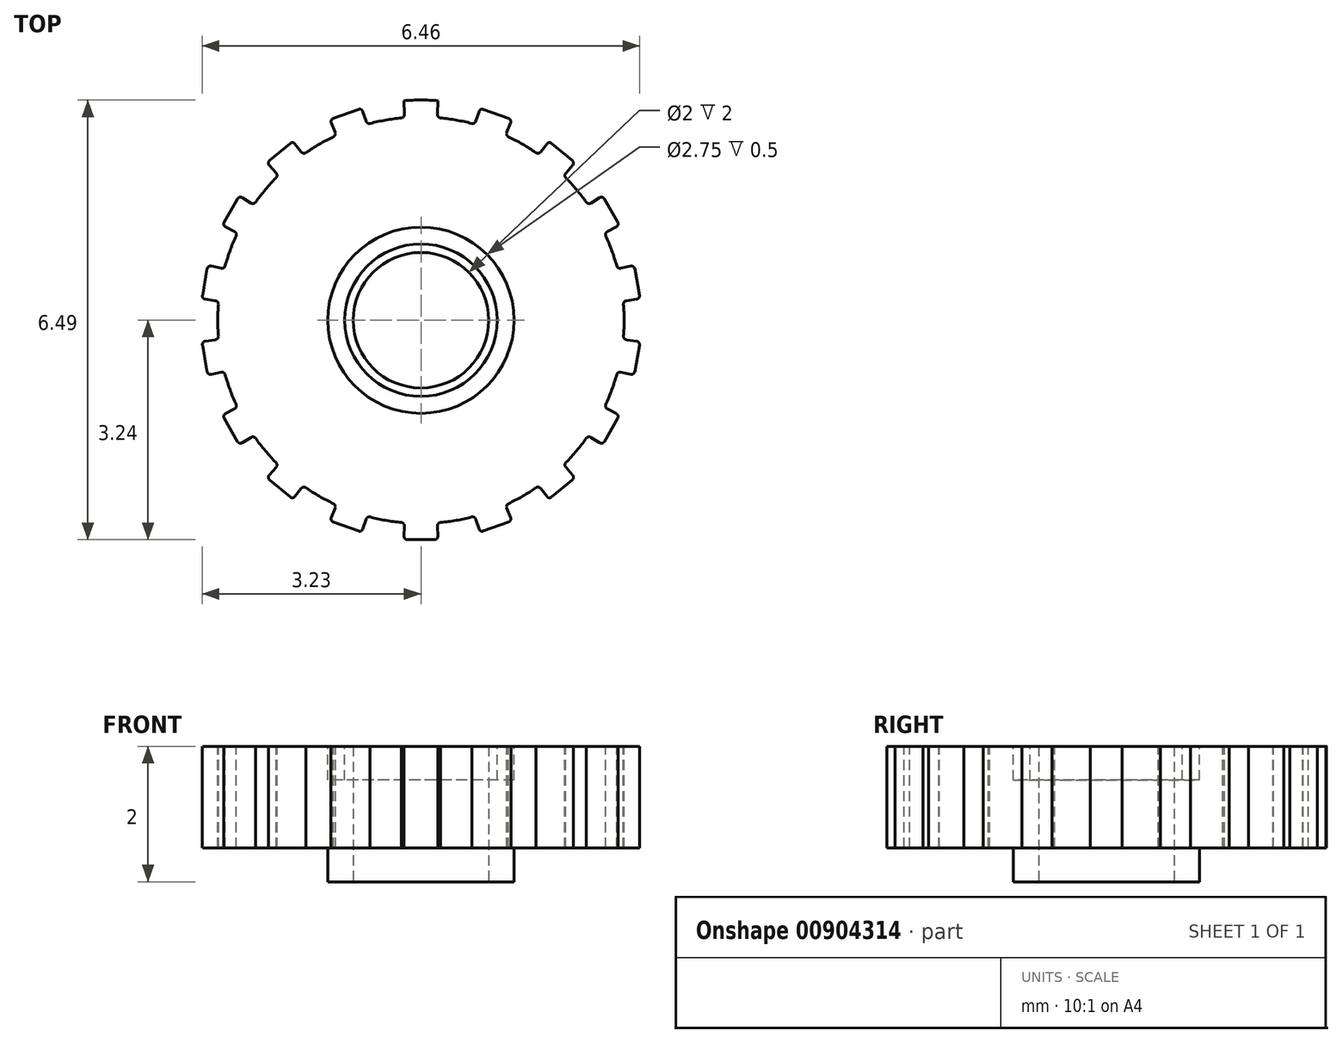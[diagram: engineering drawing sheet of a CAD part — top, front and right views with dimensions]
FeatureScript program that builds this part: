
annotation { "Feature Type Name" : "Feature", "Feature Type Description" : "" }
export const myFeature = defineFeature(function(context is Context, id is Id, definition is map)
    precondition{}
    {
        {
            var Q0;
            Q0=qCreatedBy(makeId("Front.planeOp"),FACE);
            var sketch = newSketch(context, id + "F0", { "sketchPlane" : qUnion([Q0])});
            skLineSegment(sketch, "E0.bottom", {"start": v(0, 0) * mm, "end": v(-3.25, 0) * mm});
            skLineSegment(sketch, "E0.top", {"start": v(0, 2) * mm, "end": v(-3.25, 2) * mm});
            skLineSegment(sketch, "E0.left", {"start": v(0, 0) * mm, "end": v(0, 2) * mm});
            skLineSegment(sketch, "E0.right", {"start": v(-3.25, 0) * mm, "end": v(-3.25, 2) * mm});
            skLineSegment(sketch, "E1", {"start": v(-1, 2) * mm, "end": v(-1, 0) * mm});
            skSolve(sketch);
        }
        {
            var Q0;
            {var subQ0=sQuery(id+"F0.wireOp",EDGE,"E0.right");Q0=makeQuery(id+"F0.imprint","IMPRINT",FACE,{"disambiguationData":[TD([[makeQuery(id+"F0.imprint","IMPRINT",EDGE,{"derivedFrom":subQ0}),-1.0]])]});}
            var Q1;
            Q1=sQuery(id+"F0.wireOp",EDGE,"E0.left");
            revolve(context, id + "F1", {"surfaceOperationType" : NewSurfaceOperationType.NEW, "entities" : qUnion([Q0]), "axis" : qUnion([Q1]), "revolveType" : RevolveType.FULL});
        }
        {
            var Q0;
            Q0=makeQuery(id+"F1.opRevolve","SWEPT_FACE",FACE,{"disambiguationData":[OSD([sQuery(id+"F0.wireOp",EDGE,"E0.top")])]});
            var sketch = newSketch(context, id + "F2", { "sketchPlane" : qUnion([Q0])});
            skLineSegment(sketch, "E2", {"start": v(0, 0) * mm, "end": v(0, 3.25) * mm});
            skLineSegment(sketch, "E3", {"start": v(0, 3.24) * mm, "end": v(-0.25, 3.24) * mm});
            skLineSegment(sketch, "E4", {"start": v(-0.25, 3.24) * mm, "end": v(0.25, 3.24) * mm});
            skLineSegment(sketch, "E5.bottom", {"start": v(0.12, 0) * mm, "end": v(-0.12, 0) * mm});
            skLineSegment(sketch, "E5.top", {"start": v(0.12, 0) * mm, "end": v(-0.12, 0) * mm});
            skLineSegment(sketch, "E5.left", {"start": v(0.12, 0) * mm, "end": v(0.12, 0) * mm});
            skLineSegment(sketch, "E5.right", {"start": v(-0.12, 0) * mm, "end": v(-0.12, 0) * mm});
            skPoint(sketch, "E5.middle", {"position": v(0, 0) * mm});
            skLineSegment(sketch, "E6", {"start": v(-0.25, 3.24) * mm, "end": v(-0.13, 0) * mm});
            skLineSegment(sketch, "E7", {"start": v(0.25, 3.24) * mm, "end": v(0.12, 0) * mm});
            skCircle(sketch, "E8", {"center": v(0, 0) * mm, "radius": 3 * mm});
            skLineSegment(sketch, "E9", {"start": v(-0.25, 3.24) * mm, "end": v(-0.2, 3.24) * mm});
            skLineSegment(sketch, "E10", {"start": v(-0.2, 3.24) * mm, "end": v(0.2, 3.24) * mm});
            skLineSegment(sketch, "E11", {"start": v(0.2, 3.24) * mm, "end": v(0.25, 3.24) * mm});
            skLineSegment(sketch, "E12", {"start": v(-0.2, 3.24) * mm, "end": v(-0.12, 0) * mm});
            skLineSegment(sketch, "E13", {"start": v(0.2, 3.24) * mm, "end": v(0.12, 0) * mm});
            skLineSegment(sketch, "E14", {"start": v(-0.25, 3.2) * mm, "end": v(0.25, 3.2) * mm});
            skLineSegment(sketch, "E15", {"start": v(-0.25, 3.2) * mm, "end": v(-0.3, 3.2) * mm});
            skLineSegment(sketch, "E16", {"start": v(0.25, 3.2) * mm, "end": v(0.3, 3.2) * mm});
            skLineSegment(sketch, "E17", {"start": v(-0.3, 3.2) * mm, "end": v(-0.13, 0) * mm});
            skLineSegment(sketch, "E18", {"start": v(0.3, 3.2) * mm, "end": v(0.13, 0) * mm});
            skLineSegment(sketch, "E19", {"start": v(-0.24, 3.04) * mm, "end": v(0.2, 3.04) * mm});
            skLineSegment(sketch, "E20", {"start": v(0.2, 3.04) * mm, "end": v(0.24, 3.04) * mm});
            skLineSegment(sketch, "E21", {"start": v(0.24, 3.04) * mm, "end": v(-0.2, 3.04) * mm});
            skArc(sketch, "E22", {"start": v(-0.29, 2.99) * mm, "mid": v(-0.25, 3) * mm, "end": v(-0.24, 3.04) * mm});
            skArc(sketch, "E23", {"start": v(-0.2, 3.24) * mm, "mid": v(-0.23, 3.23) * mm, "end": v(-0.25, 3.2) * mm});
            skArc(sketch, "E24", {"start": v(0.25, 3.2) * mm, "mid": v(0.23, 3.23) * mm, "end": v(0.2, 3.24) * mm});
            skArc(sketch, "E25", {"start": v(0.24, 3.04) * mm, "mid": v(0.25, 3) * mm, "end": v(0.29, 2.99) * mm});
            skArc(sketch, "E26.1.0", {"start": v(-1.3, 2.7) * mm, "mid": v(-1.27, 2.74) * mm, "end": v(-1.27, 2.77) * mm});
            skLineSegment(sketch, "E26.1.1", {"start": v(-1.34, 2.96) * mm, "end": v(-0.12, -0.04) * mm});
            skArc(sketch, "E26.1.2", {"start": v(-1.3, 2.98) * mm, "mid": v(-1.32, 2.95) * mm, "end": v(-1.32, 2.91) * mm});
            skLineSegment(sketch, "E26.1.3", {"start": v(-1.34, 2.96) * mm, "end": v(-0.87, 3.13) * mm});
            skArc(sketch, "E26.1.4", {"start": v(-0.86, 3.08) * mm, "mid": v(-0.88, 3.11) * mm, "end": v(-0.92, 3.11) * mm});
            skLineSegment(sketch, "E26.1.5", {"start": v(-0.87, 3.13) * mm, "end": v(0.12, 0.04) * mm});
            skArc(sketch, "E26.1.6", {"start": v(-0.81, 2.94) * mm, "mid": v(-0.79, 2.91) * mm, "end": v(-0.75, 2.9) * mm});
            skArc(sketch, "E26.2.0", {"start": v(-2.14, 2.1) * mm, "mid": v(-2.13, 2.14) * mm, "end": v(-2.14, 2.17) * mm});
            skLineSegment(sketch, "E26.2.1", {"start": v(-2.27, 2.32) * mm, "end": v(-0.1, -0.08) * mm});
            skArc(sketch, "E26.2.2", {"start": v(-2.24, 2.35) * mm, "mid": v(-2.25, 2.32) * mm, "end": v(-2.24, 2.28) * mm});
            skLineSegment(sketch, "E26.2.3", {"start": v(-2.27, 2.32) * mm, "end": v(-1.9, 2.64) * mm});
            skArc(sketch, "E26.2.4", {"start": v(-1.86, 2.6) * mm, "mid": v(-1.9, 2.62) * mm, "end": v(-1.93, 2.61) * mm});
            skLineSegment(sketch, "E26.2.5", {"start": v(-1.9, 2.64) * mm, "end": v(0.1, 0.08) * mm});
            skArc(sketch, "E26.2.6", {"start": v(-1.77, 2.48) * mm, "mid": v(-1.74, 2.47) * mm, "end": v(-1.7, 2.47) * mm});
            skArc(sketch, "E27.2.3.0", {"start": v(-2.73, 1.24) * mm, "mid": v(-2.73, 1.28) * mm, "end": v(-2.75, 1.31) * mm});
            skLineSegment(sketch, "E27.4.3.0", {"start": v(-2.93, 1.4) * mm, "end": v(-0.06, -0.1) * mm});
            skArc(sketch, "E27.7.3.0", {"start": v(-2.9, 1.45) * mm, "mid": v(-2.91, 1.4) * mm, "end": v(-2.89, 1.38) * mm});
            skLineSegment(sketch, "E27.11.3.0", {"start": v(-2.93, 1.4) * mm, "end": v(-2.68, 1.84) * mm});
            skArc(sketch, "E27.14.3.0", {"start": v(-2.64, 1.81) * mm, "mid": v(-2.68, 1.82) * mm, "end": v(-2.7, 1.8) * mm});
            skLineSegment(sketch, "E27.18.3.0", {"start": v(-2.68, 1.84) * mm, "end": v(0.06, 0.1) * mm});
            skArc(sketch, "E27.21.3.0", {"start": v(-2.51, 1.73) * mm, "mid": v(-2.48, 1.72) * mm, "end": v(-2.44, 1.74) * mm});
            skArc(sketch, "E27.2.4.0", {"start": v(-3, 0.24) * mm, "mid": v(-3, 0.27) * mm, "end": v(-3.04, 0.29) * mm});
            skLineSegment(sketch, "E27.4.4.0", {"start": v(-3.23, 0.32) * mm, "end": v(-0.02, -0.12) * mm});
            skArc(sketch, "E27.7.4.0", {"start": v(-3.23, 0.37) * mm, "mid": v(-3.22, 0.33) * mm, "end": v(-3.18, 0.3) * mm});
            skLineSegment(sketch, "E27.11.4.0", {"start": v(-3.23, 0.32) * mm, "end": v(-3.15, 0.8) * mm});
            skArc(sketch, "E27.14.4.0", {"start": v(-3.1, 0.8) * mm, "mid": v(-3.14, 0.8) * mm, "end": v(-3.16, 0.76) * mm});
            skLineSegment(sketch, "E27.18.4.0", {"start": v(-3.15, 0.8) * mm, "end": v(0.02, 0.12) * mm});
            skArc(sketch, "E27.21.4.0", {"start": v(-2.95, 0.77) * mm, "mid": v(-2.91, 0.77) * mm, "end": v(-2.9, 0.8) * mm});
            skArc(sketch, "E27.2.5.0", {"start": v(-2.9, -0.8) * mm, "mid": v(-2.91, -0.77) * mm, "end": v(-2.95, -0.77) * mm});
            skLineSegment(sketch, "E27.4.5.0", {"start": v(-3.15, -0.8) * mm, "end": v(0.02, -0.12) * mm});
            skArc(sketch, "E27.7.5.0", {"start": v(-3.16, -0.76) * mm, "mid": v(-3.14, -0.8) * mm, "end": v(-3.1, -0.8) * mm});
            skLineSegment(sketch, "E27.11.5.0", {"start": v(-3.15, -0.8) * mm, "end": v(-3.23, -0.32) * mm});
            skArc(sketch, "E27.14.5.0", {"start": v(-3.18, -0.3) * mm, "mid": v(-3.22, -0.33) * mm, "end": v(-3.23, -0.37) * mm});
            skLineSegment(sketch, "E27.18.5.0", {"start": v(-3.23, -0.32) * mm, "end": v(-0.02, 0.12) * mm});
            skArc(sketch, "E27.21.5.0", {"start": v(-3.04, -0.29) * mm, "mid": v(-3, -0.27) * mm, "end": v(-3, -0.24) * mm});
            skArc(sketch, "E27.2.6.0", {"start": v(-2.44, -1.74) * mm, "mid": v(-2.48, -1.72) * mm, "end": v(-2.51, -1.73) * mm});
            skLineSegment(sketch, "E27.4.6.0", {"start": v(-2.68, -1.84) * mm, "end": v(0.06, -0.1) * mm});
            skArc(sketch, "E27.7.6.0", {"start": v(-2.7, -1.8) * mm, "mid": v(-2.68, -1.82) * mm, "end": v(-2.64, -1.81) * mm});
            skLineSegment(sketch, "E27.11.6.0", {"start": v(-2.68, -1.84) * mm, "end": v(-2.93, -1.4) * mm});
            skArc(sketch, "E27.14.6.0", {"start": v(-2.89, -1.38) * mm, "mid": v(-2.91, -1.4) * mm, "end": v(-2.9, -1.45) * mm});
            skLineSegment(sketch, "E27.18.6.0", {"start": v(-2.93, -1.4) * mm, "end": v(-0.06, 0.1) * mm});
            skArc(sketch, "E27.21.6.0", {"start": v(-2.75, -1.31) * mm, "mid": v(-2.73, -1.28) * mm, "end": v(-2.73, -1.24) * mm});
            skArc(sketch, "E27.2.7.0", {"start": v(-1.7, -2.47) * mm, "mid": v(-1.74, -2.47) * mm, "end": v(-1.77, -2.48) * mm});
            skLineSegment(sketch, "E27.4.7.0", {"start": v(-1.9, -2.64) * mm, "end": v(0.1, -0.08) * mm});
            skArc(sketch, "E27.7.7.0", {"start": v(-1.93, -2.61) * mm, "mid": v(-1.9, -2.62) * mm, "end": v(-1.86, -2.6) * mm});
            skLineSegment(sketch, "E27.11.7.0", {"start": v(-1.9, -2.64) * mm, "end": v(-2.27, -2.32) * mm});
            skArc(sketch, "E27.14.7.0", {"start": v(-2.24, -2.28) * mm, "mid": v(-2.25, -2.32) * mm, "end": v(-2.24, -2.35) * mm});
            skLineSegment(sketch, "E27.18.7.0", {"start": v(-2.27, -2.32) * mm, "end": v(-0.1, 0.08) * mm});
            skArc(sketch, "E27.21.7.0", {"start": v(-2.14, -2.17) * mm, "mid": v(-2.13, -2.14) * mm, "end": v(-2.14, -2.1) * mm});
            skArc(sketch, "E28.2.8.0", {"start": v(-0.75, -2.9) * mm, "mid": v(-0.79, -2.91) * mm, "end": v(-0.81, -2.94) * mm});
            skLineSegment(sketch, "E28.4.8.0", {"start": v(-0.87, -3.13) * mm, "end": v(0.12, -0.04) * mm});
            skArc(sketch, "E28.7.8.0", {"start": v(-0.92, -3.11) * mm, "mid": v(-0.88, -3.11) * mm, "end": v(-0.86, -3.08) * mm});
            skLineSegment(sketch, "E28.11.8.0", {"start": v(-0.87, -3.13) * mm, "end": v(-1.34, -2.96) * mm});
            skArc(sketch, "E28.14.8.0", {"start": v(-1.32, -2.91) * mm, "mid": v(-1.32, -2.95) * mm, "end": v(-1.3, -2.98) * mm});
            skLineSegment(sketch, "E28.18.8.0", {"start": v(-1.34, -2.96) * mm, "end": v(-0.12, 0.04) * mm});
            skArc(sketch, "E28.21.8.0", {"start": v(-1.27, -2.77) * mm, "mid": v(-1.27, -2.74) * mm, "end": v(-1.3, -2.7) * mm});
            skArc(sketch, "E28.2.9.0", {"start": v(0.29, -2.99) * mm, "mid": v(0.25, -3) * mm, "end": v(0.24, -3.04) * mm});
            skLineSegment(sketch, "E28.4.9.0", {"start": v(0.25, -3.24) * mm, "end": v(0.12, 0) * mm});
            skArc(sketch, "E28.7.9.0", {"start": v(0.2, -3.24) * mm, "mid": v(0.23, -3.23) * mm, "end": v(0.25, -3.2) * mm});
            skLineSegment(sketch, "E28.11.9.0", {"start": v(0.25, -3.24) * mm, "end": v(-0.25, -3.24) * mm});
            skArc(sketch, "E28.14.9.0", {"start": v(-0.25, -3.2) * mm, "mid": v(-0.23, -3.23) * mm, "end": v(-0.2, -3.24) * mm});
            skLineSegment(sketch, "E28.18.9.0", {"start": v(-0.25, -3.24) * mm, "end": v(-0.13, 0) * mm});
            skArc(sketch, "E28.21.9.0", {"start": v(-0.24, -3.04) * mm, "mid": v(-0.25, -3) * mm, "end": v(-0.29, -2.99) * mm});
            skArc(sketch, "E28.2.10.0", {"start": v(1.3, -2.7) * mm, "mid": v(1.27, -2.74) * mm, "end": v(1.27, -2.77) * mm});
            skLineSegment(sketch, "E28.4.10.0", {"start": v(1.34, -2.96) * mm, "end": v(0.12, 0.04) * mm});
            skArc(sketch, "E28.7.10.0", {"start": v(1.3, -2.98) * mm, "mid": v(1.32, -2.95) * mm, "end": v(1.32, -2.91) * mm});
            skLineSegment(sketch, "E28.11.10.0", {"start": v(1.34, -2.96) * mm, "end": v(0.87, -3.13) * mm});
            skArc(sketch, "E28.14.10.0", {"start": v(0.86, -3.08) * mm, "mid": v(0.88, -3.11) * mm, "end": v(0.92, -3.11) * mm});
            skLineSegment(sketch, "E28.18.10.0", {"start": v(0.87, -3.13) * mm, "end": v(-0.12, -0.04) * mm});
            skArc(sketch, "E28.21.10.0", {"start": v(0.81, -2.94) * mm, "mid": v(0.79, -2.91) * mm, "end": v(0.75, -2.9) * mm});
            skArc(sketch, "E28.2.11.0", {"start": v(2.14, -2.1) * mm, "mid": v(2.13, -2.14) * mm, "end": v(2.14, -2.17) * mm});
            skLineSegment(sketch, "E28.4.11.0", {"start": v(2.27, -2.32) * mm, "end": v(0.1, 0.08) * mm});
            skArc(sketch, "E28.7.11.0", {"start": v(2.24, -2.35) * mm, "mid": v(2.25, -2.32) * mm, "end": v(2.24, -2.28) * mm});
            skLineSegment(sketch, "E28.11.11.0", {"start": v(2.27, -2.32) * mm, "end": v(1.9, -2.64) * mm});
            skArc(sketch, "E28.14.11.0", {"start": v(1.86, -2.6) * mm, "mid": v(1.9, -2.62) * mm, "end": v(1.93, -2.61) * mm});
            skLineSegment(sketch, "E28.18.11.0", {"start": v(1.9, -2.64) * mm, "end": v(-0.1, -0.08) * mm});
            skArc(sketch, "E28.21.11.0", {"start": v(1.77, -2.48) * mm, "mid": v(1.74, -2.47) * mm, "end": v(1.7, -2.47) * mm});
            skArc(sketch, "E28.2.12.0", {"start": v(2.73, -1.24) * mm, "mid": v(2.73, -1.28) * mm, "end": v(2.75, -1.31) * mm});
            skLineSegment(sketch, "E28.4.12.0", {"start": v(2.93, -1.4) * mm, "end": v(0.06, 0.1) * mm});
            skArc(sketch, "E28.7.12.0", {"start": v(2.9, -1.45) * mm, "mid": v(2.91, -1.4) * mm, "end": v(2.89, -1.38) * mm});
            skLineSegment(sketch, "E28.11.12.0", {"start": v(2.93, -1.4) * mm, "end": v(2.68, -1.84) * mm});
            skArc(sketch, "E28.14.12.0", {"start": v(2.64, -1.81) * mm, "mid": v(2.68, -1.82) * mm, "end": v(2.7, -1.8) * mm});
            skLineSegment(sketch, "E28.18.12.0", {"start": v(2.68, -1.84) * mm, "end": v(-0.06, -0.1) * mm});
            skArc(sketch, "E28.21.12.0", {"start": v(2.51, -1.73) * mm, "mid": v(2.48, -1.72) * mm, "end": v(2.44, -1.74) * mm});
            skArc(sketch, "E28.2.13.0", {"start": v(3, -0.24) * mm, "mid": v(3, -0.27) * mm, "end": v(3.04, -0.29) * mm});
            skLineSegment(sketch, "E28.4.13.0", {"start": v(3.23, -0.32) * mm, "end": v(0.02, 0.12) * mm});
            skArc(sketch, "E28.7.13.0", {"start": v(3.23, -0.37) * mm, "mid": v(3.22, -0.33) * mm, "end": v(3.18, -0.3) * mm});
            skLineSegment(sketch, "E28.11.13.0", {"start": v(3.23, -0.32) * mm, "end": v(3.15, -0.8) * mm});
            skArc(sketch, "E28.14.13.0", {"start": v(3.1, -0.8) * mm, "mid": v(3.14, -0.8) * mm, "end": v(3.16, -0.76) * mm});
            skLineSegment(sketch, "E28.18.13.0", {"start": v(3.15, -0.8) * mm, "end": v(-0.02, -0.12) * mm});
            skArc(sketch, "E28.21.13.0", {"start": v(2.95, -0.77) * mm, "mid": v(2.91, -0.77) * mm, "end": v(2.9, -0.8) * mm});
            skArc(sketch, "E29.2.14.0", {"start": v(2.9, 0.8) * mm, "mid": v(2.91, 0.77) * mm, "end": v(2.95, 0.77) * mm});
            skLineSegment(sketch, "E29.4.14.0", {"start": v(3.15, 0.8) * mm, "end": v(-0.02, 0.12) * mm});
            skArc(sketch, "E29.7.14.0", {"start": v(3.16, 0.76) * mm, "mid": v(3.14, 0.8) * mm, "end": v(3.1, 0.8) * mm});
            skLineSegment(sketch, "E29.11.14.0", {"start": v(3.15, 0.8) * mm, "end": v(3.23, 0.32) * mm});
            skArc(sketch, "E29.14.14.0", {"start": v(3.18, 0.3) * mm, "mid": v(3.22, 0.33) * mm, "end": v(3.23, 0.37) * mm});
            skLineSegment(sketch, "E29.18.14.0", {"start": v(3.23, 0.32) * mm, "end": v(0.02, -0.12) * mm});
            skArc(sketch, "E29.21.14.0", {"start": v(3.04, 0.29) * mm, "mid": v(3, 0.27) * mm, "end": v(3, 0.24) * mm});
            skArc(sketch, "E29.2.15.0", {"start": v(2.44, 1.74) * mm, "mid": v(2.48, 1.72) * mm, "end": v(2.51, 1.73) * mm});
            skLineSegment(sketch, "E29.4.15.0", {"start": v(2.68, 1.84) * mm, "end": v(-0.06, 0.1) * mm});
            skArc(sketch, "E29.7.15.0", {"start": v(2.7, 1.8) * mm, "mid": v(2.68, 1.82) * mm, "end": v(2.64, 1.81) * mm});
            skLineSegment(sketch, "E29.11.15.0", {"start": v(2.68, 1.84) * mm, "end": v(2.93, 1.4) * mm});
            skArc(sketch, "E29.14.15.0", {"start": v(2.89, 1.38) * mm, "mid": v(2.91, 1.4) * mm, "end": v(2.9, 1.45) * mm});
            skLineSegment(sketch, "E29.18.15.0", {"start": v(2.93, 1.4) * mm, "end": v(0.06, -0.1) * mm});
            skArc(sketch, "E29.21.15.0", {"start": v(2.75, 1.31) * mm, "mid": v(2.73, 1.28) * mm, "end": v(2.73, 1.24) * mm});
            skArc(sketch, "E30.2.16.0", {"start": v(1.7, 2.47) * mm, "mid": v(1.74, 2.47) * mm, "end": v(1.77, 2.48) * mm});
            skLineSegment(sketch, "E30.4.16.0", {"start": v(1.9, 2.64) * mm, "end": v(-0.1, 0.08) * mm});
            skArc(sketch, "E30.7.16.0", {"start": v(1.93, 2.61) * mm, "mid": v(1.9, 2.62) * mm, "end": v(1.86, 2.6) * mm});
            skLineSegment(sketch, "E30.11.16.0", {"start": v(1.9, 2.64) * mm, "end": v(2.27, 2.32) * mm});
            skArc(sketch, "E30.14.16.0", {"start": v(2.24, 2.28) * mm, "mid": v(2.25, 2.32) * mm, "end": v(2.24, 2.35) * mm});
            skLineSegment(sketch, "E30.18.16.0", {"start": v(2.27, 2.32) * mm, "end": v(0.1, -0.08) * mm});
            skArc(sketch, "E30.21.16.0", {"start": v(2.14, 2.17) * mm, "mid": v(2.13, 2.14) * mm, "end": v(2.14, 2.1) * mm});
            skArc(sketch, "E30.2.17.0", {"start": v(0.75, 2.9) * mm, "mid": v(0.79, 2.91) * mm, "end": v(0.81, 2.94) * mm});
            skLineSegment(sketch, "E30.4.17.0", {"start": v(0.87, 3.13) * mm, "end": v(-0.12, 0.04) * mm});
            skArc(sketch, "E30.7.17.0", {"start": v(0.92, 3.11) * mm, "mid": v(0.88, 3.11) * mm, "end": v(0.86, 3.08) * mm});
            skLineSegment(sketch, "E30.11.17.0", {"start": v(0.87, 3.13) * mm, "end": v(1.34, 2.96) * mm});
            skArc(sketch, "E30.14.17.0", {"start": v(1.32, 2.91) * mm, "mid": v(1.32, 2.95) * mm, "end": v(1.3, 2.98) * mm});
            skLineSegment(sketch, "E30.18.17.0", {"start": v(1.34, 2.96) * mm, "end": v(0.12, -0.04) * mm});
            skArc(sketch, "E30.21.17.0", {"start": v(1.27, 2.77) * mm, "mid": v(1.27, 2.74) * mm, "end": v(1.3, 2.7) * mm});
            skSolve(sketch);
        }
        {
            var Q0;
            {var subQ1=sQuery(id+"F2.wireOp",EDGE,"E15");Q0=makeQuery(id+"F2.imprint","IMPRINT",FACE,{"disambiguationData":[TD([[makeQuery(id+"F2.imprint","IMPRINT",EDGE,{"derivedFrom":subQ1}),-1.0]])]});}
            var Q1;
            {var subQ0=sQuery(id+"F2.wireOp",EDGE,"E15");Q1=makeQuery(id+"F2.imprint","IMPRINT",FACE,{"disambiguationData":[TD([[makeQuery(id+"F2.imprint","IMPRINT",EDGE,{"derivedFrom":subQ0}),1.0]])]});}
            var Q2;
            {var subQ0=sQuery(id+"F2.wireOp",EDGE,"E9");Q2=makeQuery(id+"F2.imprint","IMPRINT",FACE,{"disambiguationData":[TD([[makeQuery(id+"F2.imprint","IMPRINT",EDGE,{"derivedFrom":subQ0}),-1.0]])]});}
            var Q3;
            {var subQ5=sQuery(id+"F2.wireOp",EDGE,"E9");Q3=makeQuery(id+"F2.imprint","IMPRINT",FACE,{"disambiguationData":[TD([[makeQuery(id+"F2.imprint","IMPRINT",EDGE,{"derivedFrom":subQ5}),1.0]])]});}
            var Q4;
            {var subQ5=sQuery(id+"F2.wireOp",EDGE,"E11");Q4=makeQuery(id+"F2.imprint","IMPRINT",FACE,{"disambiguationData":[TD([[makeQuery(id+"F2.imprint","IMPRINT",EDGE,{"derivedFrom":subQ5}),1.0]])]});}
            var Q5;
            {var subQ0=sQuery(id+"F2.wireOp",EDGE,"E11");Q5=makeQuery(id+"F2.imprint","IMPRINT",FACE,{"disambiguationData":[TD([[makeQuery(id+"F2.imprint","IMPRINT",EDGE,{"derivedFrom":subQ0}),-1.0]])]});}
            var Q6;
            {var subQ0=sQuery(id+"F2.wireOp",EDGE,"E16");Q6=makeQuery(id+"F2.imprint","IMPRINT",FACE,{"disambiguationData":[TD([[makeQuery(id+"F2.imprint","IMPRINT",EDGE,{"derivedFrom":subQ0}),1.0]])]});}
            var Q7;
            {var subQ0=sQuery(id+"F2.wireOp",EDGE,"E16");Q7=makeQuery(id+"F2.imprint","IMPRINT",FACE,{"disambiguationData":[TD([[makeQuery(id+"F2.imprint","IMPRINT",EDGE,{"derivedFrom":subQ0}),-1.0]])]});}
            var Q8;
            {var subQ3=sQuery(id+"F2.wireOp",EDGE,"E27.7.7.0");Q8=makeQuery(id+"F2.imprint","IMPRINT",FACE,{"disambiguationData":[TD([[makeQuery(id+"F2.imprint","IMPRINT",EDGE,{"derivedFrom":subQ3}),-1.0]])]});}
            var Q9;
            {var subQ0=sQuery(id+"F2.wireOp",EDGE,"E27.11.7.0");var subQ3=makeQuery(id+"F2.imprint","INTERSECT",VERTEX,{"derivedFrom":[sQuery(id+"F2.wireOp",EDGE,"E27.7.7.0"),subQ0]});Q9=makeQuery(id+"F2.imprint","IMPRINT",FACE,{"disambiguationData":[TD([[makeQuery(id+"F2.imprint","IMPRINT",EDGE,{"disambiguationData":[TD([[subQ3,-1.0]])],"derivedFrom":subQ0}),1.0]])]});}
            var Q10;
            {var subQ3=sQuery(id+"F2.wireOp",EDGE,"E27.14.7.0");Q10=makeQuery(id+"F2.imprint","IMPRINT",FACE,{"disambiguationData":[TD([[makeQuery(id+"F2.imprint","IMPRINT",EDGE,{"derivedFrom":subQ3}),-1.0]])]});}
            var Q11;
            {var subQ4=sQuery(id+"F2.wireOp",EDGE,"E27.2.6.0");Q11=makeQuery(id+"F2.imprint","IMPRINT",FACE,{"disambiguationData":[TD([[makeQuery(id+"F2.imprint","IMPRINT",EDGE,{"derivedFrom":subQ4}),1.0]])]});}
            var Q12;
            {var subQ3=sQuery(id+"F2.wireOp",EDGE,"E27.7.6.0");Q12=makeQuery(id+"F2.imprint","IMPRINT",FACE,{"disambiguationData":[TD([[makeQuery(id+"F2.imprint","IMPRINT",EDGE,{"derivedFrom":subQ3}),-1.0]])]});}
            var Q13;
            {var subQ0=sQuery(id+"F2.wireOp",EDGE,"E27.11.6.0");var subQ3=makeQuery(id+"F2.imprint","INTERSECT",VERTEX,{"derivedFrom":[sQuery(id+"F2.wireOp",EDGE,"E27.7.6.0"),subQ0]});Q13=makeQuery(id+"F2.imprint","IMPRINT",FACE,{"disambiguationData":[TD([[makeQuery(id+"F2.imprint","IMPRINT",EDGE,{"disambiguationData":[TD([[subQ3,-1.0]])],"derivedFrom":subQ0}),1.0]])]});}
            var Q14;
            {var subQ1=sQuery(id+"F2.wireOp",EDGE,"E27.2.5.0");Q14=makeQuery(id+"F2.imprint","IMPRINT",FACE,{"disambiguationData":[TD([[makeQuery(id+"F2.imprint","IMPRINT",EDGE,{"derivedFrom":subQ1}),1.0]])]});}
            var Q15;
            {var subQ3=sQuery(id+"F2.wireOp",EDGE,"E27.14.6.0");Q15=makeQuery(id+"F2.imprint","IMPRINT",FACE,{"disambiguationData":[TD([[makeQuery(id+"F2.imprint","IMPRINT",EDGE,{"derivedFrom":subQ3}),-1.0]])]});}
            var Q16;
            {var subQ0=sQuery(id+"F2.wireOp",EDGE,"E27.11.5.0");var subQ3=makeQuery(id+"F2.imprint","INTERSECT",VERTEX,{"derivedFrom":[sQuery(id+"F2.wireOp",EDGE,"E27.7.5.0"),subQ0]});Q16=makeQuery(id+"F2.imprint","IMPRINT",FACE,{"disambiguationData":[TD([[makeQuery(id+"F2.imprint","IMPRINT",EDGE,{"disambiguationData":[TD([[subQ3,-1.0]])],"derivedFrom":subQ0}),1.0]])]});}
            var Q17;
            {var subQ3=sQuery(id+"F2.wireOp",EDGE,"E27.7.5.0");Q17=makeQuery(id+"F2.imprint","IMPRINT",FACE,{"disambiguationData":[TD([[makeQuery(id+"F2.imprint","IMPRINT",EDGE,{"derivedFrom":subQ3}),-1.0]])]});}
            var Q18;
            {var subQ3=sQuery(id+"F2.wireOp",EDGE,"E27.14.5.0");Q18=makeQuery(id+"F2.imprint","IMPRINT",FACE,{"disambiguationData":[TD([[makeQuery(id+"F2.imprint","IMPRINT",EDGE,{"derivedFrom":subQ3}),-1.0]])]});}
            var Q19;
            {var subQ4=sQuery(id+"F2.wireOp",EDGE,"E27.2.4.0");Q19=makeQuery(id+"F2.imprint","IMPRINT",FACE,{"disambiguationData":[TD([[makeQuery(id+"F2.imprint","IMPRINT",EDGE,{"derivedFrom":subQ4}),1.0]])]});}
            var Q20;
            {var subQ3=sQuery(id+"F2.wireOp",EDGE,"E27.7.4.0");Q20=makeQuery(id+"F2.imprint","IMPRINT",FACE,{"disambiguationData":[TD([[makeQuery(id+"F2.imprint","IMPRINT",EDGE,{"derivedFrom":subQ3}),-1.0]])]});}
            var Q21;
            {var subQ0=sQuery(id+"F2.wireOp",EDGE,"E27.11.4.0");var subQ3=makeQuery(id+"F2.imprint","INTERSECT",VERTEX,{"derivedFrom":[sQuery(id+"F2.wireOp",EDGE,"E27.7.4.0"),subQ0]});Q21=makeQuery(id+"F2.imprint","IMPRINT",FACE,{"disambiguationData":[TD([[makeQuery(id+"F2.imprint","IMPRINT",EDGE,{"disambiguationData":[TD([[subQ3,-1.0]])],"derivedFrom":subQ0}),1.0]])]});}
            var Q22;
            {var subQ3=sQuery(id+"F2.wireOp",EDGE,"E27.14.4.0");Q22=makeQuery(id+"F2.imprint","IMPRINT",FACE,{"disambiguationData":[TD([[makeQuery(id+"F2.imprint","IMPRINT",EDGE,{"derivedFrom":subQ3}),-1.0]])]});}
            var Q23;
            {var subQ1=sQuery(id+"F2.wireOp",EDGE,"E27.2.3.0");Q23=makeQuery(id+"F2.imprint","IMPRINT",FACE,{"disambiguationData":[TD([[makeQuery(id+"F2.imprint","IMPRINT",EDGE,{"derivedFrom":subQ1}),1.0]])]});}
            var Q24;
            {var subQ3=sQuery(id+"F2.wireOp",EDGE,"E27.7.3.0");Q24=makeQuery(id+"F2.imprint","IMPRINT",FACE,{"disambiguationData":[TD([[makeQuery(id+"F2.imprint","IMPRINT",EDGE,{"derivedFrom":subQ3}),-1.0]])]});}
            var Q25;
            {var subQ0=sQuery(id+"F2.wireOp",EDGE,"E27.11.3.0");var subQ3=makeQuery(id+"F2.imprint","INTERSECT",VERTEX,{"derivedFrom":[sQuery(id+"F2.wireOp",EDGE,"E27.7.3.0"),subQ0]});Q25=makeQuery(id+"F2.imprint","IMPRINT",FACE,{"disambiguationData":[TD([[makeQuery(id+"F2.imprint","IMPRINT",EDGE,{"disambiguationData":[TD([[subQ3,-1.0]])],"derivedFrom":subQ0}),1.0]])]});}
            var Q26;
            {var subQ3=sQuery(id+"F2.wireOp",EDGE,"E27.14.3.0");Q26=makeQuery(id+"F2.imprint","IMPRINT",FACE,{"disambiguationData":[TD([[makeQuery(id+"F2.imprint","IMPRINT",EDGE,{"derivedFrom":subQ3}),-1.0]])]});}
            var Q27;
            {var subQ0=sQuery(id+"F2.wireOp",EDGE,"E26.2.3");var subQ3=makeQuery(id+"F2.imprint","INTERSECT",VERTEX,{"derivedFrom":[sQuery(id+"F2.wireOp",EDGE,"E26.2.2"),subQ0]});Q27=makeQuery(id+"F2.imprint","IMPRINT",FACE,{"disambiguationData":[TD([[makeQuery(id+"F2.imprint","IMPRINT",EDGE,{"disambiguationData":[TD([[subQ3,-1.0]])],"derivedFrom":subQ0}),1.0]])]});}
            var Q28;
            {var subQ3=sQuery(id+"F2.wireOp",EDGE,"E26.2.2");Q28=makeQuery(id+"F2.imprint","IMPRINT",FACE,{"disambiguationData":[TD([[makeQuery(id+"F2.imprint","IMPRINT",EDGE,{"derivedFrom":subQ3}),-1.0]])]});}
            var Q29;
            {var subQ1=sQuery(id+"F2.wireOp",EDGE,"E26.2.0");Q29=makeQuery(id+"F2.imprint","IMPRINT",FACE,{"disambiguationData":[TD([[makeQuery(id+"F2.imprint","IMPRINT",EDGE,{"derivedFrom":subQ1}),1.0]])]});}
            var Q30;
            {var subQ3=sQuery(id+"F2.wireOp",EDGE,"E26.2.4");Q30=makeQuery(id+"F2.imprint","IMPRINT",FACE,{"disambiguationData":[TD([[makeQuery(id+"F2.imprint","IMPRINT",EDGE,{"derivedFrom":subQ3}),-1.0]])]});}
            var Q31;
            {var subQ1=sQuery(id+"F2.wireOp",EDGE,"E26.1.0");Q31=makeQuery(id+"F2.imprint","IMPRINT",FACE,{"disambiguationData":[TD([[makeQuery(id+"F2.imprint","IMPRINT",EDGE,{"derivedFrom":subQ1}),1.0]])]});}
            var Q32;
            {var subQ3=sQuery(id+"F2.wireOp",EDGE,"E26.1.2");Q32=makeQuery(id+"F2.imprint","IMPRINT",FACE,{"disambiguationData":[TD([[makeQuery(id+"F2.imprint","IMPRINT",EDGE,{"derivedFrom":subQ3}),-1.0]])]});}
            var Q33;
            {var subQ3=sQuery(id+"F2.wireOp",EDGE,"E26.1.4");Q33=makeQuery(id+"F2.imprint","IMPRINT",FACE,{"disambiguationData":[TD([[makeQuery(id+"F2.imprint","IMPRINT",EDGE,{"derivedFrom":subQ3}),-1.0]])]});}
            var Q34;
            {var subQ0=sQuery(id+"F2.wireOp",EDGE,"E26.1.3");var subQ3=makeQuery(id+"F2.imprint","INTERSECT",VERTEX,{"derivedFrom":[sQuery(id+"F2.wireOp",EDGE,"E26.1.2"),subQ0]});Q34=makeQuery(id+"F2.imprint","IMPRINT",FACE,{"disambiguationData":[TD([[makeQuery(id+"F2.imprint","IMPRINT",EDGE,{"disambiguationData":[TD([[subQ3,-1.0]])],"derivedFrom":subQ0}),1.0]])]});}
            var Q35;
            {var subQ3=sQuery(id+"F2.wireOp",EDGE,"E28.7.13.0");Q35=makeQuery(id+"F2.imprint","IMPRINT",FACE,{"disambiguationData":[TD([[makeQuery(id+"F2.imprint","IMPRINT",EDGE,{"derivedFrom":subQ3}),-1.0]])]});}
            var Q36;
            {var subQ0=sQuery(id+"F2.wireOp",EDGE,"E28.11.13.0");var subQ3=makeQuery(id+"F2.imprint","INTERSECT",VERTEX,{"derivedFrom":[sQuery(id+"F2.wireOp",EDGE,"E28.7.13.0"),subQ0]});Q36=makeQuery(id+"F2.imprint","IMPRINT",FACE,{"disambiguationData":[TD([[makeQuery(id+"F2.imprint","IMPRINT",EDGE,{"disambiguationData":[TD([[subQ3,-1.0]])],"derivedFrom":subQ0}),1.0]])]});}
            var Q37;
            {var subQ3=sQuery(id+"F2.wireOp",EDGE,"E28.14.13.0");Q37=makeQuery(id+"F2.imprint","IMPRINT",FACE,{"disambiguationData":[TD([[makeQuery(id+"F2.imprint","IMPRINT",EDGE,{"derivedFrom":subQ3}),-1.0]])]});}
            var Q38;
            {var subQ1=sQuery(id+"F2.wireOp",EDGE,"E28.2.12.0");Q38=makeQuery(id+"F2.imprint","IMPRINT",FACE,{"disambiguationData":[TD([[makeQuery(id+"F2.imprint","IMPRINT",EDGE,{"derivedFrom":subQ1}),1.0]])]});}
            var Q39;
            {var subQ3=sQuery(id+"F2.wireOp",EDGE,"E28.7.12.0");Q39=makeQuery(id+"F2.imprint","IMPRINT",FACE,{"disambiguationData":[TD([[makeQuery(id+"F2.imprint","IMPRINT",EDGE,{"derivedFrom":subQ3}),-1.0]])]});}
            var Q40;
            {var subQ0=sQuery(id+"F2.wireOp",EDGE,"E28.11.12.0");var subQ3=makeQuery(id+"F2.imprint","INTERSECT",VERTEX,{"derivedFrom":[sQuery(id+"F2.wireOp",EDGE,"E28.7.12.0"),subQ0]});Q40=makeQuery(id+"F2.imprint","IMPRINT",FACE,{"disambiguationData":[TD([[makeQuery(id+"F2.imprint","IMPRINT",EDGE,{"disambiguationData":[TD([[subQ3,-1.0]])],"derivedFrom":subQ0}),1.0]])]});}
            var Q41;
            {var subQ3=sQuery(id+"F2.wireOp",EDGE,"E28.14.12.0");Q41=makeQuery(id+"F2.imprint","IMPRINT",FACE,{"disambiguationData":[TD([[makeQuery(id+"F2.imprint","IMPRINT",EDGE,{"derivedFrom":subQ3}),-1.0]])]});}
            var Q42;
            {var subQ1=sQuery(id+"F2.wireOp",EDGE,"E28.2.11.0");Q42=makeQuery(id+"F2.imprint","IMPRINT",FACE,{"disambiguationData":[TD([[makeQuery(id+"F2.imprint","IMPRINT",EDGE,{"derivedFrom":subQ1}),1.0]])]});}
            var Q43;
            {var subQ3=sQuery(id+"F2.wireOp",EDGE,"E28.7.11.0");Q43=makeQuery(id+"F2.imprint","IMPRINT",FACE,{"disambiguationData":[TD([[makeQuery(id+"F2.imprint","IMPRINT",EDGE,{"derivedFrom":subQ3}),-1.0]])]});}
            var Q44;
            {var subQ0=sQuery(id+"F2.wireOp",EDGE,"E28.11.11.0");var subQ3=makeQuery(id+"F2.imprint","INTERSECT",VERTEX,{"derivedFrom":[sQuery(id+"F2.wireOp",EDGE,"E28.7.11.0"),subQ0]});Q44=makeQuery(id+"F2.imprint","IMPRINT",FACE,{"disambiguationData":[TD([[makeQuery(id+"F2.imprint","IMPRINT",EDGE,{"disambiguationData":[TD([[subQ3,-1.0]])],"derivedFrom":subQ0}),1.0]])]});}
            var Q45;
            {var subQ3=sQuery(id+"F2.wireOp",EDGE,"E28.7.10.0");Q45=makeQuery(id+"F2.imprint","IMPRINT",FACE,{"disambiguationData":[TD([[makeQuery(id+"F2.imprint","IMPRINT",EDGE,{"derivedFrom":subQ3}),-1.0]])]});}
            var Q46;
            {var subQ0=sQuery(id+"F2.wireOp",EDGE,"E28.11.10.0");var subQ3=makeQuery(id+"F2.imprint","INTERSECT",VERTEX,{"derivedFrom":[sQuery(id+"F2.wireOp",EDGE,"E28.7.10.0"),subQ0]});Q46=makeQuery(id+"F2.imprint","IMPRINT",FACE,{"disambiguationData":[TD([[makeQuery(id+"F2.imprint","IMPRINT",EDGE,{"disambiguationData":[TD([[subQ3,-1.0]])],"derivedFrom":subQ0}),1.0]])]});}
            var Q47;
            {var subQ3=sQuery(id+"F2.wireOp",EDGE,"E28.7.9.0");Q47=makeQuery(id+"F2.imprint","IMPRINT",FACE,{"disambiguationData":[TD([[makeQuery(id+"F2.imprint","IMPRINT",EDGE,{"derivedFrom":subQ3}),-1.0]])]});}
            var Q48;
            {var subQ0=sQuery(id+"F2.wireOp",EDGE,"E28.11.9.0");var subQ3=makeQuery(id+"F2.imprint","INTERSECT",VERTEX,{"derivedFrom":[sQuery(id+"F2.wireOp",EDGE,"E28.7.9.0"),subQ0]});Q48=makeQuery(id+"F2.imprint","IMPRINT",FACE,{"disambiguationData":[TD([[makeQuery(id+"F2.imprint","IMPRINT",EDGE,{"disambiguationData":[TD([[subQ3,-1.0]])],"derivedFrom":subQ0}),1.0]])]});}
            var Q49;
            {var subQ3=sQuery(id+"F2.wireOp",EDGE,"E28.14.9.0");Q49=makeQuery(id+"F2.imprint","IMPRINT",FACE,{"disambiguationData":[TD([[makeQuery(id+"F2.imprint","IMPRINT",EDGE,{"derivedFrom":subQ3}),-1.0]])]});}
            var Q50;
            {var subQ1=sQuery(id+"F2.wireOp",EDGE,"E28.2.8.0");Q50=makeQuery(id+"F2.imprint","IMPRINT",FACE,{"disambiguationData":[TD([[makeQuery(id+"F2.imprint","IMPRINT",EDGE,{"derivedFrom":subQ1}),1.0]])]});}
            var Q51;
            {var subQ1=sQuery(id+"F2.wireOp",EDGE,"E28.2.9.0");Q51=makeQuery(id+"F2.imprint","IMPRINT",FACE,{"disambiguationData":[TD([[makeQuery(id+"F2.imprint","IMPRINT",EDGE,{"derivedFrom":subQ1}),1.0]])]});}
            var Q52;
            {var subQ1=sQuery(id+"F2.wireOp",EDGE,"E28.2.10.0");Q52=makeQuery(id+"F2.imprint","IMPRINT",FACE,{"disambiguationData":[TD([[makeQuery(id+"F2.imprint","IMPRINT",EDGE,{"derivedFrom":subQ1}),1.0]])]});}
            var Q53;
            {var subQ3=sQuery(id+"F2.wireOp",EDGE,"E28.14.10.0");Q53=makeQuery(id+"F2.imprint","IMPRINT",FACE,{"disambiguationData":[TD([[makeQuery(id+"F2.imprint","IMPRINT",EDGE,{"derivedFrom":subQ3}),-1.0]])]});}
            var Q54;
            {var subQ3=sQuery(id+"F2.wireOp",EDGE,"E28.14.11.0");Q54=makeQuery(id+"F2.imprint","IMPRINT",FACE,{"disambiguationData":[TD([[makeQuery(id+"F2.imprint","IMPRINT",EDGE,{"derivedFrom":subQ3}),-1.0]])]});}
            var Q55;
            {var subQ3=sQuery(id+"F2.wireOp",EDGE,"E28.7.8.0");Q55=makeQuery(id+"F2.imprint","IMPRINT",FACE,{"disambiguationData":[TD([[makeQuery(id+"F2.imprint","IMPRINT",EDGE,{"derivedFrom":subQ3}),-1.0]])]});}
            var Q56;
            {var subQ0=sQuery(id+"F2.wireOp",EDGE,"E28.11.8.0");var subQ3=makeQuery(id+"F2.imprint","INTERSECT",VERTEX,{"derivedFrom":[sQuery(id+"F2.wireOp",EDGE,"E28.7.8.0"),subQ0]});Q56=makeQuery(id+"F2.imprint","IMPRINT",FACE,{"disambiguationData":[TD([[makeQuery(id+"F2.imprint","IMPRINT",EDGE,{"disambiguationData":[TD([[subQ3,-1.0]])],"derivedFrom":subQ0}),1.0]])]});}
            var Q57;
            {var subQ3=sQuery(id+"F2.wireOp",EDGE,"E28.14.8.0");Q57=makeQuery(id+"F2.imprint","IMPRINT",FACE,{"disambiguationData":[TD([[makeQuery(id+"F2.imprint","IMPRINT",EDGE,{"derivedFrom":subQ3}),-1.0]])]});}
            var Q58;
            {var subQ1=sQuery(id+"F2.wireOp",EDGE,"E27.2.7.0");Q58=makeQuery(id+"F2.imprint","IMPRINT",FACE,{"disambiguationData":[TD([[makeQuery(id+"F2.imprint","IMPRINT",EDGE,{"derivedFrom":subQ1}),1.0]])]});}
            var Q59;
            {var subQ4=sQuery(id+"F2.wireOp",EDGE,"E28.2.13.0");Q59=makeQuery(id+"F2.imprint","IMPRINT",FACE,{"disambiguationData":[TD([[makeQuery(id+"F2.imprint","IMPRINT",EDGE,{"derivedFrom":subQ4}),1.0]])]});}
            var Q60;
            {var subQ3=sQuery(id+"F2.wireOp",EDGE,"E29.14.14.0");Q60=makeQuery(id+"F2.imprint","IMPRINT",FACE,{"disambiguationData":[TD([[makeQuery(id+"F2.imprint","IMPRINT",EDGE,{"derivedFrom":subQ3}),-1.0]])]});}
            var Q61;
            {var subQ0=sQuery(id+"F2.wireOp",EDGE,"E29.11.14.0");var subQ3=makeQuery(id+"F2.imprint","INTERSECT",VERTEX,{"derivedFrom":[sQuery(id+"F2.wireOp",EDGE,"E29.7.14.0"),subQ0]});Q61=makeQuery(id+"F2.imprint","IMPRINT",FACE,{"disambiguationData":[TD([[makeQuery(id+"F2.imprint","IMPRINT",EDGE,{"disambiguationData":[TD([[subQ3,-1.0]])],"derivedFrom":subQ0}),1.0]])]});}
            var Q62;
            {var subQ3=sQuery(id+"F2.wireOp",EDGE,"E29.7.14.0");Q62=makeQuery(id+"F2.imprint","IMPRINT",FACE,{"disambiguationData":[TD([[makeQuery(id+"F2.imprint","IMPRINT",EDGE,{"derivedFrom":subQ3}),-1.0]])]});}
            var Q63;
            {var subQ1=sQuery(id+"F2.wireOp",EDGE,"E29.2.14.0");Q63=makeQuery(id+"F2.imprint","IMPRINT",FACE,{"disambiguationData":[TD([[makeQuery(id+"F2.imprint","IMPRINT",EDGE,{"derivedFrom":subQ1}),1.0]])]});}
            var Q64;
            {var subQ0=sQuery(id+"F2.wireOp",EDGE,"E29.11.15.0");var subQ3=makeQuery(id+"F2.imprint","INTERSECT",VERTEX,{"derivedFrom":[sQuery(id+"F2.wireOp",EDGE,"E29.7.15.0"),subQ0]});Q64=makeQuery(id+"F2.imprint","IMPRINT",FACE,{"disambiguationData":[TD([[makeQuery(id+"F2.imprint","IMPRINT",EDGE,{"disambiguationData":[TD([[subQ3,-1.0]])],"derivedFrom":subQ0}),1.0]])]});}
            var Q65;
            {var subQ3=sQuery(id+"F2.wireOp",EDGE,"E29.7.15.0");Q65=makeQuery(id+"F2.imprint","IMPRINT",FACE,{"disambiguationData":[TD([[makeQuery(id+"F2.imprint","IMPRINT",EDGE,{"derivedFrom":subQ3}),-1.0]])]});}
            var Q66;
            {var subQ3=sQuery(id+"F2.wireOp",EDGE,"E29.14.15.0");Q66=makeQuery(id+"F2.imprint","IMPRINT",FACE,{"disambiguationData":[TD([[makeQuery(id+"F2.imprint","IMPRINT",EDGE,{"derivedFrom":subQ3}),-1.0]])]});}
            var Q67;
            {var subQ0=sQuery(id+"F2.wireOp",EDGE,"E30.11.17.0");var subQ3=makeQuery(id+"F2.imprint","INTERSECT",VERTEX,{"derivedFrom":[sQuery(id+"F2.wireOp",EDGE,"E30.7.17.0"),subQ0]});Q67=makeQuery(id+"F2.imprint","IMPRINT",FACE,{"disambiguationData":[TD([[makeQuery(id+"F2.imprint","IMPRINT",EDGE,{"disambiguationData":[TD([[subQ3,-1.0]])],"derivedFrom":subQ0}),1.0]])]});}
            var Q68;
            {var subQ3=sQuery(id+"F2.wireOp",EDGE,"E30.7.17.0");Q68=makeQuery(id+"F2.imprint","IMPRINT",FACE,{"disambiguationData":[TD([[makeQuery(id+"F2.imprint","IMPRINT",EDGE,{"derivedFrom":subQ3}),-1.0]])]});}
            var Q69;
            {var subQ3=sQuery(id+"F2.wireOp",EDGE,"E30.14.17.0");Q69=makeQuery(id+"F2.imprint","IMPRINT",FACE,{"disambiguationData":[TD([[makeQuery(id+"F2.imprint","IMPRINT",EDGE,{"derivedFrom":subQ3}),-1.0]])]});}
            var Q70;
            {var subQ7=sQuery(id+"F2.wireOp",EDGE,"E30.2.16.0");Q70=makeQuery(id+"F2.imprint","IMPRINT",FACE,{"disambiguationData":[TD([[makeQuery(id+"F2.imprint","IMPRINT",EDGE,{"derivedFrom":subQ7}),1.0]])]});}
            var Q71;
            {var subQ0=sQuery(id+"F2.wireOp",EDGE,"E30.11.16.0");var subQ3=makeQuery(id+"F2.imprint","INTERSECT",VERTEX,{"derivedFrom":[sQuery(id+"F2.wireOp",EDGE,"E30.7.16.0"),subQ0]});Q71=makeQuery(id+"F2.imprint","IMPRINT",FACE,{"disambiguationData":[TD([[makeQuery(id+"F2.imprint","IMPRINT",EDGE,{"disambiguationData":[TD([[subQ3,-1.0]])],"derivedFrom":subQ0}),1.0]])]});}
            var Q72;
            {var subQ3=sQuery(id+"F2.wireOp",EDGE,"E30.7.16.0");Q72=makeQuery(id+"F2.imprint","IMPRINT",FACE,{"disambiguationData":[TD([[makeQuery(id+"F2.imprint","IMPRINT",EDGE,{"derivedFrom":subQ3}),-1.0]])]});}
            var Q73;
            {var subQ3=sQuery(id+"F2.wireOp",EDGE,"E30.14.16.0");Q73=makeQuery(id+"F2.imprint","IMPRINT",FACE,{"disambiguationData":[TD([[makeQuery(id+"F2.imprint","IMPRINT",EDGE,{"derivedFrom":subQ3}),-1.0]])]});}
            var Q74;
            {var subQ1=sQuery(id+"F2.wireOp",EDGE,"E29.2.15.0");Q74=makeQuery(id+"F2.imprint","IMPRINT",FACE,{"disambiguationData":[TD([[makeQuery(id+"F2.imprint","IMPRINT",EDGE,{"derivedFrom":subQ1}),1.0]])]});}
            extrude(context, id + "F3", {"entities" : qUnion([Q0, Q1, Q2, Q3, Q4, Q5, Q6, Q7, Q8, Q9, Q10, Q11, Q12, Q13, Q14, Q15, Q16, Q17, Q18, Q19, Q20, Q21, Q22, Q23, Q24, Q25, Q26, Q27, Q28, Q29, Q30, Q31, Q32, Q33, Q34, Q35, Q36, Q37, Q38, Q39, Q40, Q41, Q42, Q43, Q44, Q45, Q46, Q47, Q48, Q49, Q50, Q51, Q52, Q53, Q54, Q55, Q56, Q57, Q58, Q59, Q60, Q61, Q62, Q63, Q64, Q65, Q66, Q67, Q68, Q69, Q70, Q71, Q72, Q73, Q74]), "operationType" : NewBodyOperationType.REMOVE, "oppositeDirection" : true, "depth" : 25 * mm, "offsetDistance" : 25 * mm});
        }
        {
            var Q0;
            Q0=makeQuery(id+"F1.opRevolve","SWEPT_FACE",FACE,{"disambiguationData":[OSD([sQuery(id+"F0.wireOp",EDGE,"E0.top")])]});
            var sketch = newSketch(context, id + "F4", { "sketchPlane" : qUnion([Q0])});
            skCircle(sketch, "E31", {"center": v(0, 0) * mm, "radius": 1.13 * mm});
            skCircle(sketch, "E32", {"center": v(0, 0) * mm, "radius": 1.38 * mm});
            skSolve(sketch);
        }
        {
            var Q0;
            Q0=makeQuery(id+"F1.opRevolve","SWEPT_FACE",FACE,{"disambiguationData":[OSD([sQuery(id+"F0.wireOp",EDGE,"E0.bottom")])]});
            var sketch = newSketch(context, id + "F5", { "sketchPlane" : qUnion([Q0])});
            skCircle(sketch, "E33.0", {"center": v(0, 0) * mm, "radius": 1.38 * mm});
            skCircle(sketch, "E34.0", {"center": v(0, 0) * mm, "radius": 1.13 * mm});
            skSolve(sketch);
        }
        {
            var Q0;
            Q0=makeQuery(id+"F5.imprint","IMPRINT",FACE,{"disambiguationData":[TD([[makeQuery(id+"F5.imprint","IMPRINT",EDGE,{"derivedFrom":sQuery(id+"F5.wireOp",EDGE,"E33.0")}),-1.0]])]});
            extrude(context, id + "F6", {"entities" : qUnion([Q0]), "operationType" : NewBodyOperationType.REMOVE, "oppositeDirection" : true, "depth" : 0.5 * mm, "offsetDistance" : 25 * mm});
        }
        {
            var Q0;
            Q0=makeQuery(id+"F4.imprint","IMPRINT",FACE,{"disambiguationData":[TD([[makeQuery(id+"F4.imprint","IMPRINT",EDGE,{"derivedFrom":sQuery(id+"F4.wireOp",EDGE,"E31")}),-1.0]])]});
            extrude(context, id + "F7", {"entities" : qUnion([Q0]), "operationType" : NewBodyOperationType.REMOVE, "oppositeDirection" : true, "depth" : 0.5 * mm, "offsetDistance" : 25 * mm});
        }
    });
